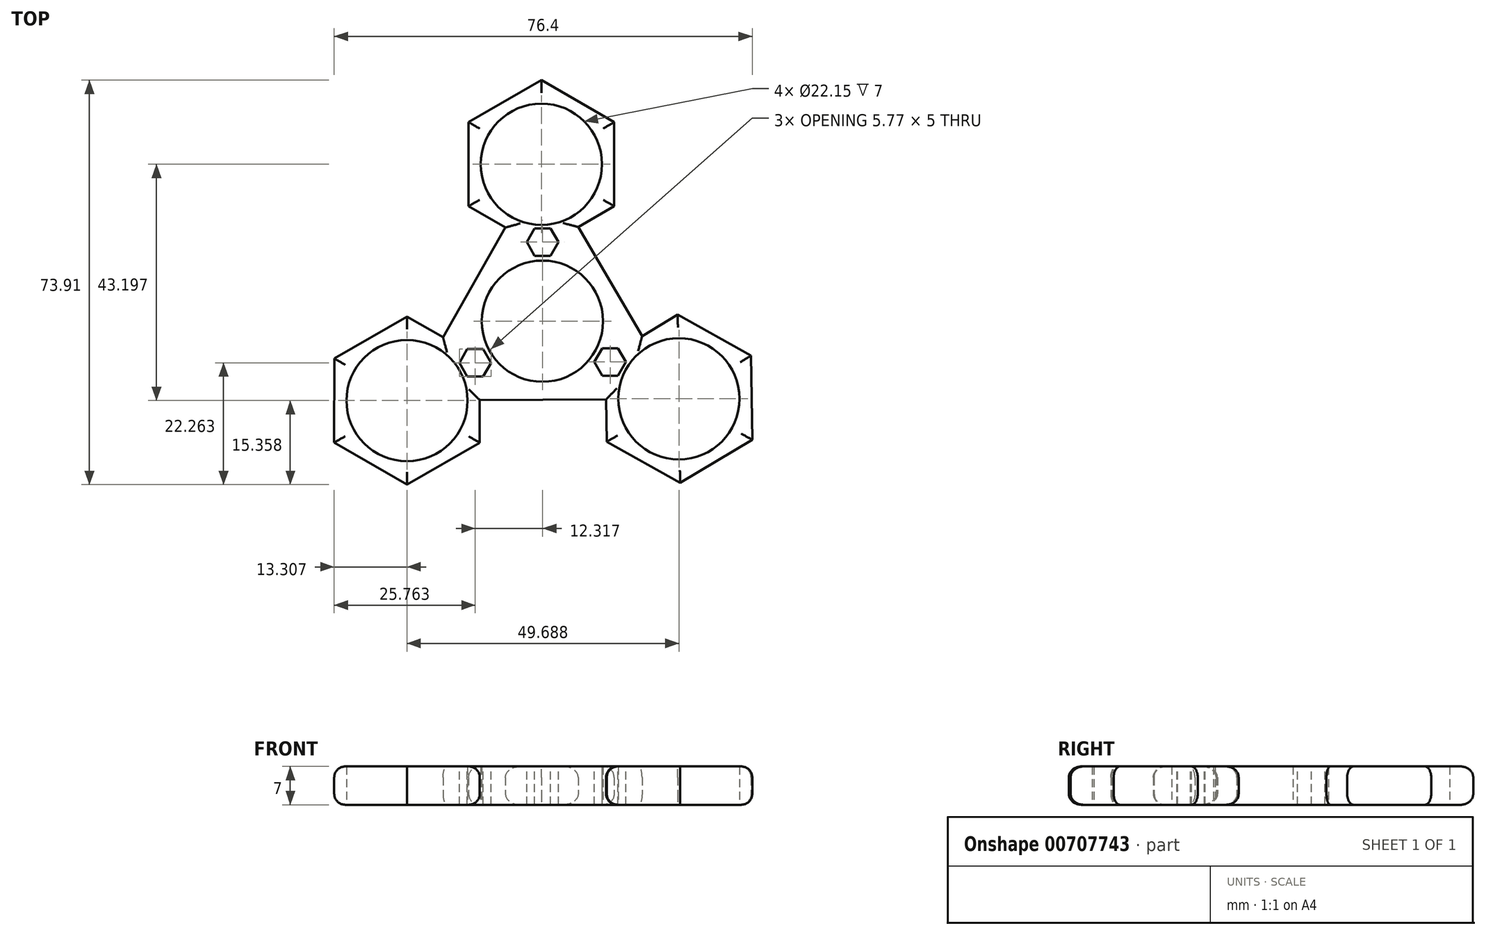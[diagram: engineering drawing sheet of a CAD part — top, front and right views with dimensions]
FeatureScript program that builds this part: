
annotation { "Feature Type Name" : "Feature", "Feature Type Description" : "" }
export const myFeature = defineFeature(function(context is Context, id is Id, definition is map)
    precondition{}
    {
        {
            var Q0;
            Q0=qCreatedBy(makeId("Top.planeOp"),FACE);
            var sketch = newSketch(context, id + "F0", { "sketchPlane" : qUnion([Q0])});
            skCircle(sketch, "E0.cCircle", {"center": v(-0.02, -0.21) * mm, "radius": 14.34 * mm, "construction": true});
            skLineSegment(sketch, "E0.0", {"start": v(-0.22, 28.47) * mm, "end": v(24.91, -14.4) * mm});
            skLineSegment(sketch, "E0.1", {"start": v(24.91, -14.4) * mm, "end": v(-24.77, -14.72) * mm});
            skLineSegment(sketch, "E0.2", {"start": v(-24.77, -14.72) * mm, "end": v(-0.22, 28.47) * mm});
            skPoint(sketch, "E0.0.midPoint", {"position": v(12.35, 7.04) * mm});
            skCircle(sketch, "E1.cCircle", {"center": v(-0.22, 28.47) * mm, "radius": 13.3 * mm, "construction": true});
            skLineSegment(sketch, "E1.0", {"start": v(13.08, 36.15) * mm, "end": v(13.08, 20.8) * mm});
            skLineSegment(sketch, "E1.1", {"start": v(13.08, 20.8) * mm, "end": v(-0.22, 13.12) * mm});
            skLineSegment(sketch, "E1.2", {"start": v(-0.22, 13.12) * mm, "end": v(-13.51, 20.8) * mm});
            skLineSegment(sketch, "E1.3", {"start": v(-13.51, 20.8) * mm, "end": v(-13.51, 36.15) * mm});
            skLineSegment(sketch, "E1.4", {"start": v(-13.51, 36.15) * mm, "end": v(-0.22, 43.83) * mm});
            skLineSegment(sketch, "E1.5", {"start": v(-0.22, 43.83) * mm, "end": v(13.08, 36.15) * mm});
            skPoint(sketch, "E1.0.midPoint", {"position": v(13.08, 28.47) * mm});
            skCircle(sketch, "E2.cCircle", {"center": v(24.91, -14.4) * mm, "radius": 13.3 * mm, "construction": true});
            skLineSegment(sketch, "E2.0", {"start": v(38.1, -6.53) * mm, "end": v(38.32, -21.88) * mm});
            skLineSegment(sketch, "E2.1", {"start": v(38.32, -21.88) * mm, "end": v(25.13, -29.74) * mm});
            skLineSegment(sketch, "E2.2", {"start": v(25.13, -29.74) * mm, "end": v(11.73, -22.26) * mm});
            skLineSegment(sketch, "E2.3", {"start": v(11.73, -22.26) * mm, "end": v(11.5, -6.9) * mm});
            skLineSegment(sketch, "E2.4", {"start": v(11.5, -6.9) * mm, "end": v(24.7, 0.96) * mm});
            skLineSegment(sketch, "E2.5", {"start": v(24.7, 0.96) * mm, "end": v(38.1, -6.53) * mm});
            skPoint(sketch, "E2.0.midPoint", {"position": v(38.21, -14.2) * mm});
            skCircle(sketch, "E3.cCircle", {"center": v(-24.77, -14.72) * mm, "radius": 13.3 * mm, "construction": true});
            skLineSegment(sketch, "E3.0", {"start": v(-24.79, -30.08) * mm, "end": v(-38.08, -22.39) * mm});
            skLineSegment(sketch, "E3.1", {"start": v(-38.08, -22.39) * mm, "end": v(-38.06, -7.03) * mm});
            skLineSegment(sketch, "E3.2", {"start": v(-38.06, -7.03) * mm, "end": v(-24.76, 0.63) * mm});
            skLineSegment(sketch, "E3.3", {"start": v(-24.76, 0.63) * mm, "end": v(-11.47, -7.06) * mm});
            skLineSegment(sketch, "E3.4", {"start": v(-11.47, -7.06) * mm, "end": v(-11.48, -22.41) * mm});
            skLineSegment(sketch, "E3.5", {"start": v(-11.48, -22.41) * mm, "end": v(-24.79, -30.08) * mm});
            skPoint(sketch, "E3.0.midPoint", {"position": v(-31.43, -26.23) * mm});
            skCircle(sketch, "E4", {"center": v(-0.22, 28.47) * mm, "radius": 11.07 * mm});
            skCircle(sketch, "E5", {"center": v(-0.02, -0.21) * mm, "radius": 11.07 * mm});
            skCircle(sketch, "E6", {"center": v(-24.77, -14.72) * mm, "radius": 11.07 * mm});
            skCircle(sketch, "E7", {"center": v(24.91, -14.4) * mm, "radius": 11.07 * mm});
            skSolve(sketch);
        }
        {
            var Q0;
            {var subQ0=sQuery(id+"F0.wireOp",EDGE,"E1.0");Q0=makeQuery(id+"F0.imprint","IMPRINT",FACE,{"disambiguationData":[TD([[makeQuery(id+"F0.imprint","IMPRINT",EDGE,{"derivedFrom":subQ0}),-1.0]])]});}
            var Q1;
            {var subQ1=sQuery(id+"F0.wireOp",EDGE,"E1.1");var subQ3=sQuery(id+"F0.wireOp",EDGE,"E0.0");var subQ4=makeQuery(id+"F0.imprint","INTERSECT",VERTEX,{"derivedFrom":[subQ3,subQ1]});Q1=makeQuery(id+"F0.imprint","IMPRINT",FACE,{"disambiguationData":[TD([[makeQuery(id+"F0.imprint","IMPRINT",EDGE,{"disambiguationData":[TD([[subQ4,1.0]])],"derivedFrom":subQ3}),-1.0]])]});}
            var Q2;
            Q2=makeQuery(id+"F0.imprint","IMPRINT",FACE,{"disambiguationData":[TD([[makeQuery(id+"F0.imprint","IMPRINT",EDGE,{"derivedFrom":sQuery(id+"F0.wireOp",EDGE,"E5")}),-1.0]])]});
            var Q3;
            {var subQ0=sQuery(id+"F0.wireOp",EDGE,"E2.4");var subQ7=sQuery(id+"F0.wireOp",EDGE,"E0.0");var subQ8=makeQuery(id+"F0.imprint","INTERSECT",VERTEX,{"derivedFrom":[subQ7,subQ0]});Q3=makeQuery(id+"F0.imprint","IMPRINT",FACE,{"disambiguationData":[TD([[makeQuery(id+"F0.imprint","IMPRINT",EDGE,{"disambiguationData":[TD([[subQ8,-1.0]])],"derivedFrom":subQ7}),-1.0]])]});}
            var Q4;
            {var subQ0=sQuery(id+"F0.wireOp",EDGE,"E3.4");var subQ5=sQuery(id+"F0.wireOp",EDGE,"E0.1");var subQ6=makeQuery(id+"F0.imprint","INTERSECT",VERTEX,{"derivedFrom":[subQ5,subQ0]});Q4=makeQuery(id+"F0.imprint","IMPRINT",FACE,{"disambiguationData":[TD([[makeQuery(id+"F0.imprint","IMPRINT",EDGE,{"disambiguationData":[TD([[subQ6,-1.0]])],"derivedFrom":subQ5}),-1.0]])]});}
            var Q5;
            Q5=makeQuery(id+"F0.imprint","IMPRINT",FACE,{"disambiguationData":[TD([[makeQuery(id+"F0.imprint","IMPRINT",EDGE,{"derivedFrom":sQuery(id+"F0.wireOp",EDGE,"E3.0")}),-1.0]])]});
            var Q6;
            Q6=makeQuery(id+"F0.imprint","IMPRINT",FACE,{"disambiguationData":[TD([[makeQuery(id+"F0.imprint","IMPRINT",EDGE,{"derivedFrom":sQuery(id+"F0.wireOp",EDGE,"E2.0")}),-1.0]])]});
            extrude(context, id + "F1", {"entities" : qUnion([Q0, Q1, Q2, Q3, Q4, Q5, Q6]), "depth" : 7 * mm, "offsetDistance" : 25 * mm});
        }
        {
            var Q0;
            Q0=makeQuery(id+"F1.opExtrude","CAP_EDGE",EDGE,{"disambiguationData":[OSD([sQuery(id+"F0.wireOp",EDGE,"E1.2")])],"isStart":false});
            var Q1;
            Q1=makeQuery(id+"F1.opExtrude","CAP_EDGE",EDGE,{"disambiguationData":[OSD([sQuery(id+"F0.wireOp",EDGE,"E1.3")])],"isStart":false});
            var Q2;
            Q2=makeQuery(id+"F1.opExtrude","CAP_EDGE",EDGE,{"disambiguationData":[OSD([sQuery(id+"F0.wireOp",EDGE,"E1.4")])],"isStart":false});
            var Q3;
            Q3=makeQuery(id+"F1.opExtrude","CAP_EDGE",EDGE,{"disambiguationData":[OSD([sQuery(id+"F0.wireOp",EDGE,"E1.5")])],"isStart":false});
            var Q4;
            Q4=makeQuery(id+"F1.opExtrude","CAP_EDGE",EDGE,{"disambiguationData":[OSD([sQuery(id+"F0.wireOp",EDGE,"E1.0")])],"isStart":false});
            var Q5;
            Q5=makeQuery(id+"F1.opExtrude","CAP_EDGE",EDGE,{"disambiguationData":[OSD([sQuery(id+"F0.wireOp",EDGE,"E0.0")])],"isStart":false});
            var Q6;
            Q6=makeQuery(id+"F1.opExtrude","CAP_EDGE",EDGE,{"disambiguationData":[OSD([sQuery(id+"F0.wireOp",EDGE,"E1.1")])],"isStart":false});
            var Q7;
            Q7=makeQuery(id+"F1.opExtrude","CAP_EDGE",EDGE,{"disambiguationData":[OSD([sQuery(id+"F0.wireOp",EDGE,"E2.4")])],"isStart":false});
            var Q8;
            Q8=makeQuery(id+"F1.opExtrude","CAP_EDGE",EDGE,{"disambiguationData":[OSD([sQuery(id+"F0.wireOp",EDGE,"E2.5")])],"isStart":false});
            var Q9;
            Q9=makeQuery(id+"F1.opExtrude","CAP_EDGE",EDGE,{"disambiguationData":[OSD([sQuery(id+"F0.wireOp",EDGE,"E2.0")])],"isStart":false});
            var Q10;
            Q10=makeQuery(id+"F1.opExtrude","CAP_EDGE",EDGE,{"disambiguationData":[OSD([sQuery(id+"F0.wireOp",EDGE,"E2.1")])],"isStart":false});
            var Q11;
            Q11=makeQuery(id+"F1.opExtrude","CAP_EDGE",EDGE,{"disambiguationData":[OSD([sQuery(id+"F0.wireOp",EDGE,"E2.2")])],"isStart":false});
            var Q12;
            Q12=makeQuery(id+"F1.opExtrude","CAP_EDGE",EDGE,{"disambiguationData":[OSD([sQuery(id+"F0.wireOp",EDGE,"E2.3")])],"isStart":false});
            var Q13;
            Q13=makeQuery(id+"F1.opExtrude","CAP_EDGE",EDGE,{"disambiguationData":[OSD([sQuery(id+"F0.wireOp",EDGE,"E0.1")])],"isStart":false});
            var Q14;
            Q14=makeQuery(id+"F1.opExtrude","CAP_EDGE",EDGE,{"disambiguationData":[OSD([sQuery(id+"F0.wireOp",EDGE,"E3.4")])],"isStart":false});
            var Q15;
            Q15=makeQuery(id+"F1.opExtrude","CAP_EDGE",EDGE,{"disambiguationData":[OSD([sQuery(id+"F0.wireOp",EDGE,"E3.0")])],"isStart":false});
            var Q16;
            Q16=makeQuery(id+"F1.opExtrude","CAP_EDGE",EDGE,{"disambiguationData":[OSD([sQuery(id+"F0.wireOp",EDGE,"E3.5")])],"isStart":false});
            var Q17;
            Q17=makeQuery(id+"F1.opExtrude","CAP_EDGE",EDGE,{"disambiguationData":[OSD([sQuery(id+"F0.wireOp",EDGE,"E3.1")])],"isStart":false});
            var Q18;
            Q18=makeQuery(id+"F1.opExtrude","CAP_EDGE",EDGE,{"disambiguationData":[OSD([sQuery(id+"F0.wireOp",EDGE,"E3.2")])],"isStart":false});
            var Q19;
            Q19=makeQuery(id+"F1.opExtrude","CAP_EDGE",EDGE,{"disambiguationData":[OSD([sQuery(id+"F0.wireOp",EDGE,"E3.3")])],"isStart":false});
            var Q20;
            Q20=makeQuery(id+"F1.opExtrude","CAP_EDGE",EDGE,{"disambiguationData":[OSD([sQuery(id+"F0.wireOp",EDGE,"E0.2")])],"isStart":false});
            var Q21;
            Q21=makeQuery(id+"F1.opExtrude","CAP_EDGE",EDGE,{"disambiguationData":[OSD([sQuery(id+"F0.wireOp",EDGE,"E2.1")])],"isStart":true});
            var Q22;
            Q22=makeQuery(id+"F1.opExtrude","CAP_EDGE",EDGE,{"disambiguationData":[OSD([sQuery(id+"F0.wireOp",EDGE,"E2.0")])],"isStart":true});
            var Q23;
            Q23=makeQuery(id+"F1.opExtrude","CAP_EDGE",EDGE,{"disambiguationData":[OSD([sQuery(id+"F0.wireOp",EDGE,"E2.5")])],"isStart":true});
            var Q24;
            Q24=makeQuery(id+"F1.opExtrude","CAP_EDGE",EDGE,{"disambiguationData":[OSD([sQuery(id+"F0.wireOp",EDGE,"E2.4")])],"isStart":true});
            var Q25;
            Q25=makeQuery(id+"F1.opExtrude","CAP_EDGE",EDGE,{"disambiguationData":[OSD([sQuery(id+"F0.wireOp",EDGE,"E2.2")])],"isStart":true});
            var Q26;
            Q26=makeQuery(id+"F1.opExtrude","CAP_EDGE",EDGE,{"disambiguationData":[OSD([sQuery(id+"F0.wireOp",EDGE,"E2.3")])],"isStart":true});
            var Q27;
            Q27=makeQuery(id+"F1.opExtrude","CAP_EDGE",EDGE,{"disambiguationData":[OSD([sQuery(id+"F0.wireOp",EDGE,"E0.0")])],"isStart":true});
            var Q28;
            Q28=makeQuery(id+"F1.opExtrude","CAP_EDGE",EDGE,{"disambiguationData":[OSD([sQuery(id+"F0.wireOp",EDGE,"E0.1")])],"isStart":true});
            var Q29;
            Q29=makeQuery(id+"F1.opExtrude","CAP_EDGE",EDGE,{"disambiguationData":[OSD([sQuery(id+"F0.wireOp",EDGE,"E1.1")])],"isStart":true});
            var Q30;
            Q30=makeQuery(id+"F1.opExtrude","CAP_EDGE",EDGE,{"disambiguationData":[OSD([sQuery(id+"F0.wireOp",EDGE,"E1.0")])],"isStart":true});
            var Q31;
            Q31=makeQuery(id+"F1.opExtrude","CAP_EDGE",EDGE,{"disambiguationData":[OSD([sQuery(id+"F0.wireOp",EDGE,"E1.5")])],"isStart":true});
            var Q32;
            Q32=makeQuery(id+"F1.opExtrude","CAP_EDGE",EDGE,{"disambiguationData":[OSD([sQuery(id+"F0.wireOp",EDGE,"E1.4")])],"isStart":true});
            var Q33;
            Q33=makeQuery(id+"F1.opExtrude","CAP_EDGE",EDGE,{"disambiguationData":[OSD([sQuery(id+"F0.wireOp",EDGE,"E1.3")])],"isStart":true});
            var Q34;
            Q34=makeQuery(id+"F1.opExtrude","CAP_EDGE",EDGE,{"disambiguationData":[OSD([sQuery(id+"F0.wireOp",EDGE,"E1.2")])],"isStart":true});
            var Q35;
            Q35=makeQuery(id+"F1.opExtrude","CAP_EDGE",EDGE,{"disambiguationData":[OSD([sQuery(id+"F0.wireOp",EDGE,"E0.2")])],"isStart":true});
            var Q36;
            Q36=makeQuery(id+"F1.opExtrude","CAP_EDGE",EDGE,{"disambiguationData":[OSD([sQuery(id+"F0.wireOp",EDGE,"E3.3")])],"isStart":true});
            var Q37;
            Q37=makeQuery(id+"F1.opExtrude","CAP_EDGE",EDGE,{"disambiguationData":[OSD([sQuery(id+"F0.wireOp",EDGE,"E3.2")])],"isStart":true});
            var Q38;
            Q38=makeQuery(id+"F1.opExtrude","CAP_EDGE",EDGE,{"disambiguationData":[OSD([sQuery(id+"F0.wireOp",EDGE,"E3.1")])],"isStart":true});
            var Q39;
            Q39=makeQuery(id+"F1.opExtrude","CAP_EDGE",EDGE,{"disambiguationData":[OSD([sQuery(id+"F0.wireOp",EDGE,"E3.0")])],"isStart":true});
            var Q40;
            Q40=makeQuery(id+"F1.opExtrude","CAP_EDGE",EDGE,{"disambiguationData":[OSD([sQuery(id+"F0.wireOp",EDGE,"E3.5")])],"isStart":true});
            var Q41;
            Q41=makeQuery(id+"F1.opExtrude","CAP_EDGE",EDGE,{"disambiguationData":[OSD([sQuery(id+"F0.wireOp",EDGE,"E3.4")])],"isStart":true});
            fillet(context, id + "F2", {"entities" : qUnion([Q0, Q1, Q2, Q3, Q4, Q5, Q6, Q7, Q8, Q9, Q10, Q11, Q12, Q13, Q14, Q15, Q16, Q17, Q18, Q19, Q20, Q21, Q22, Q23, Q24, Q25, Q26, Q27, Q28, Q29, Q30, Q31, Q32, Q33, Q34, Q35, Q36, Q37, Q38, Q39, Q40, Q41]), "radius" : 2 * mm, "tangentPropagation" : true, "allowEdgeOverflow" : false});
        }
        {
            var Q0;
            Q0=makeQuery(id+"F1.opExtrude","CAP_FACE",FACE,{"disambiguationData":[OSD([sQuery(id+"F0.wireOp",EDGE,"E0.0"),sQuery(id+"F0.wireOp",EDGE,"E0.1"),sQuery(id+"F0.wireOp",EDGE,"E0.2"),sQuery(id+"F0.wireOp",EDGE,"E1.0"),sQuery(id+"F0.wireOp",EDGE,"E1.1"),sQuery(id+"F0.wireOp",EDGE,"E1.2"),sQuery(id+"F0.wireOp",EDGE,"E1.3"),sQuery(id+"F0.wireOp",EDGE,"E1.4"),sQuery(id+"F0.wireOp",EDGE,"E1.5"),sQuery(id+"F0.wireOp",EDGE,"E2.0"),sQuery(id+"F0.wireOp",EDGE,"E2.1"),sQuery(id+"F0.wireOp",EDGE,"E2.2"),sQuery(id+"F0.wireOp",EDGE,"E2.3"),sQuery(id+"F0.wireOp",EDGE,"E2.4"),sQuery(id+"F0.wireOp",EDGE,"E2.5"),sQuery(id+"F0.wireOp",EDGE,"E3.0"),sQuery(id+"F0.wireOp",EDGE,"E3.1"),sQuery(id+"F0.wireOp",EDGE,"E3.2"),sQuery(id+"F0.wireOp",EDGE,"E3.3"),sQuery(id+"F0.wireOp",EDGE,"E3.4"),sQuery(id+"F0.wireOp",EDGE,"E3.5"),sQuery(id+"F0.wireOp",EDGE,"E4"),sQuery(id+"F0.wireOp",EDGE,"E5"),sQuery(id+"F0.wireOp",EDGE,"E6"),sQuery(id+"F0.wireOp",EDGE,"E7")])],"isStart":false});
            var sketch = newSketch(context, id + "F3", { "sketchPlane" : qUnion([Q0])});
            skCircle(sketch, "E8.cCircle", {"center": v(0, 14.24) * mm, "radius": 2.5 * mm, "construction": true});
            skLineSegment(sketch, "E8.0", {"start": v(-1.44, 16.74) * mm, "end": v(1.44, 16.74) * mm});
            skLineSegment(sketch, "E8.1", {"start": v(1.44, 16.74) * mm, "end": v(2.89, 14.24) * mm});
            skLineSegment(sketch, "E8.2", {"start": v(2.89, 14.24) * mm, "end": v(1.44, 11.74) * mm});
            skLineSegment(sketch, "E8.3", {"start": v(1.44, 11.74) * mm, "end": v(-1.44, 11.74) * mm});
            skLineSegment(sketch, "E8.4", {"start": v(-1.44, 11.74) * mm, "end": v(-2.89, 14.24) * mm});
            skLineSegment(sketch, "E8.5", {"start": v(-2.89, 14.24) * mm, "end": v(-1.44, 16.74) * mm});
            skPoint(sketch, "E8.0.midPoint", {"position": v(0, 16.74) * mm});
            skCircle(sketch, "E9.cCircle", {"center": v(12.35, -7.67) * mm, "radius": 2.5 * mm, "construction": true});
            skLineSegment(sketch, "E9.0", {"start": v(10.91, -5.17) * mm, "end": v(13.8, -5.17) * mm});
            skLineSegment(sketch, "E9.1", {"start": v(13.8, -5.17) * mm, "end": v(15.24, -7.67) * mm});
            skLineSegment(sketch, "E9.2", {"start": v(15.24, -7.67) * mm, "end": v(13.8, -10.17) * mm});
            skLineSegment(sketch, "E9.3", {"start": v(13.8, -10.17) * mm, "end": v(10.91, -10.17) * mm});
            skLineSegment(sketch, "E9.4", {"start": v(10.91, -10.17) * mm, "end": v(9.47, -7.67) * mm});
            skLineSegment(sketch, "E9.5", {"start": v(9.47, -7.67) * mm, "end": v(10.91, -5.17) * mm});
            skPoint(sketch, "E9.0.midPoint", {"position": v(12.35, -5.17) * mm});
            skCircle(sketch, "E10.cCircle", {"center": v(-12.32, -7.82) * mm, "radius": 2.5 * mm, "construction": true});
            skLineSegment(sketch, "E10.0", {"start": v(-13.76, -5.32) * mm, "end": v(-10.87, -5.32) * mm});
            skLineSegment(sketch, "E10.1", {"start": v(-10.87, -5.32) * mm, "end": v(-9.43, -7.82) * mm});
            skLineSegment(sketch, "E10.2", {"start": v(-9.43, -7.82) * mm, "end": v(-10.87, -10.32) * mm});
            skLineSegment(sketch, "E10.3", {"start": v(-10.87, -10.32) * mm, "end": v(-13.76, -10.32) * mm});
            skLineSegment(sketch, "E10.4", {"start": v(-13.76, -10.32) * mm, "end": v(-15.2, -7.82) * mm});
            skLineSegment(sketch, "E10.5", {"start": v(-15.2, -7.82) * mm, "end": v(-13.76, -5.32) * mm});
            skPoint(sketch, "E10.0.midPoint", {"position": v(-12.32, -5.32) * mm});
            skSolve(sketch);
        }
        {
            var Q0;
            Q0=makeQuery(id+"F3.imprint","IMPRINT",FACE,{"disambiguationData":[TD([[makeQuery(id+"F3.imprint","IMPRINT",EDGE,{"derivedFrom":sQuery(id+"F3.wireOp",EDGE,"E8.0")}),-1.0]])]});
            var Q1;
            Q1=makeQuery(id+"F3.imprint","IMPRINT",FACE,{"disambiguationData":[TD([[makeQuery(id+"F3.imprint","IMPRINT",EDGE,{"derivedFrom":sQuery(id+"F3.wireOp",EDGE,"6fd5247a-20b5-4970-8771-11870c1da40a.0")}),-1.0]])]});
            var Q2;
            Q2=makeQuery(id+"F3.imprint","IMPRINT",FACE,{"disambiguationData":[TD([[makeQuery(id+"F3.imprint","IMPRINT",EDGE,{"derivedFrom":sQuery(id+"F3.wireOp",EDGE,"7bccf8e0-6ca9-4a5c-a14e-cb17776c03df.0")}),-1.0]])]});
            var Q3;
            Q3=makeQuery(id+"F3.imprint","IMPRINT",FACE,{"disambiguationData":[TD([[makeQuery(id+"F3.imprint","IMPRINT",EDGE,{"derivedFrom":sQuery(id+"F3.wireOp",EDGE,"E10.0")}),-1.0]])]});
            var Q4;
            Q4=makeQuery(id+"F3.imprint","IMPRINT",FACE,{"disambiguationData":[TD([[makeQuery(id+"F3.imprint","IMPRINT",EDGE,{"derivedFrom":sQuery(id+"F3.wireOp",EDGE,"E9.0")}),-1.0]])]});
            extrude(context, id + "F4", {"entities" : qUnion([Q0, Q1, Q2, Q3, Q4]), "operationType" : NewBodyOperationType.REMOVE, "oppositeDirection" : true, "depth" : 25 * mm, "offsetDistance" : 25 * mm});
        }
    });
